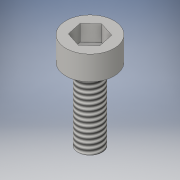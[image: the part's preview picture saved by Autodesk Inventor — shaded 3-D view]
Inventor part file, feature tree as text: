
AUTODESK INVENTOR PART (.ipt)
format: ipt  version: 2016 SP1 (Build 200210100, 210)  size: 118,272 bytes
history: native  units: in
note: dims shown in document units (in); Inventor stores cm internally (conversion verified against a paired STEP export)
features: extrude x3, sketch x3, thread x1
ambient origin geometry x8: Origin, YZ Plane, XZ Plane, XY Plane, X Axis, Y Axis, Z Axis, Center Point
bodies: Solid1 (feature_tree)
feature tree (7):
  extrude  "Extrusion1"  Depth=0.25in
  thread  "Thread1"  [1 undecoded]
  extrude  "Extrusion2"  Depth=0.25in
  extrude  "Extrusion3"  [1 undecoded]
  sketch  "Sketch1"  dims[d0=0.75in d1=0.0in d2=0.25in d3=1.0in d4=0.0in]
  sketch  "Sketch2"  dims[d5=0.25in d6=0.0in d7=0.5in]
  sketch  "Sketch3"  dims[d8=0.17in d9=0.0in]
note: 2 required parameter values undecoded (feature->parameter linkage not recoverable at this tier; creation-order binding heuristic only, values carry confidence <= 0.55)
